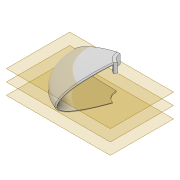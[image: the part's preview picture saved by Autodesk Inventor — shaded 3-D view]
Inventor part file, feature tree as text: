
AUTODESK INVENTOR PART (.ipt)
format: ipt  version: 2022 (Build 260153000, 153)  size: 450,560 bytes
history: native  units: mm
features: extrude x6, sketch x6, projected_geometry x4, plane x3, shell x1, revolve x1, fillet x1
ambient origin geometry x8: Origin, YZ Plane, XZ Plane, XY Plane, X Axis, Y Axis, Z Axis, Center Point
bodies: Solid1 (feature_tree)
feature tree (22):
  extrude  "Extrusion1"  Depth=2.0mm
  shell  "Shell1"  Thickness=80.0mm
  extrude  "Extrusion16"  Depth=12.217305mm
  revolve  "Revolution2"  [1 undecoded]
  extrude  "Extrusion17"  Depth=100.0mm TaperAngle=0.0deg
  plane  "Work Plane4"
  plane  "Work Plane5"
  plane  "Work Plane6"
  sketch  "Sketch41"  dims[d173=4.0mm d174=13.1mm d175=0.0mm]
  extrude  "Extrusion18"  Depth=13.1mm TaperAngle=0.0deg
  extrude  "Extrusion19"  Depth=100.0mm TaperAngle=0.0deg
  extrude  "Extrusion20"  Depth=1.5mm
  fillet  "Fillet5"  [1 undecoded]
  sketch  "Sketch3"  dims[d0=1.0mm d1=0.0mm d2=2.0mm d159=80.0mm]
  sketch  "Sketch37"  dims[d160=10.0mm d161=0.0mm d163=12.217305mm]
  sketch  "Sketch39"  dims[d164=1.0mm d165=0.0mm d166=6.454mm d167=16.2mm d168=-16.2mm]
  projected_geometry  "Projected Loop21"
  sketch  "Sketch40"  dims[d169=33.2mm d170=100.0mm d171=0.0mm]
  projected_geometry  "Projected Loop22"
  sketch  "Sketch42"  dims[d176=36.0mm d177=100.0mm d178=0.0mm d187=1.5mm]
  projected_geometry  "Project Cut Edges1"
  projected_geometry  "Project Cut Edges2"
note: 2 required parameter values undecoded (feature->parameter linkage not recoverable at this tier; creation-order binding heuristic only, values carry confidence <= 0.55)